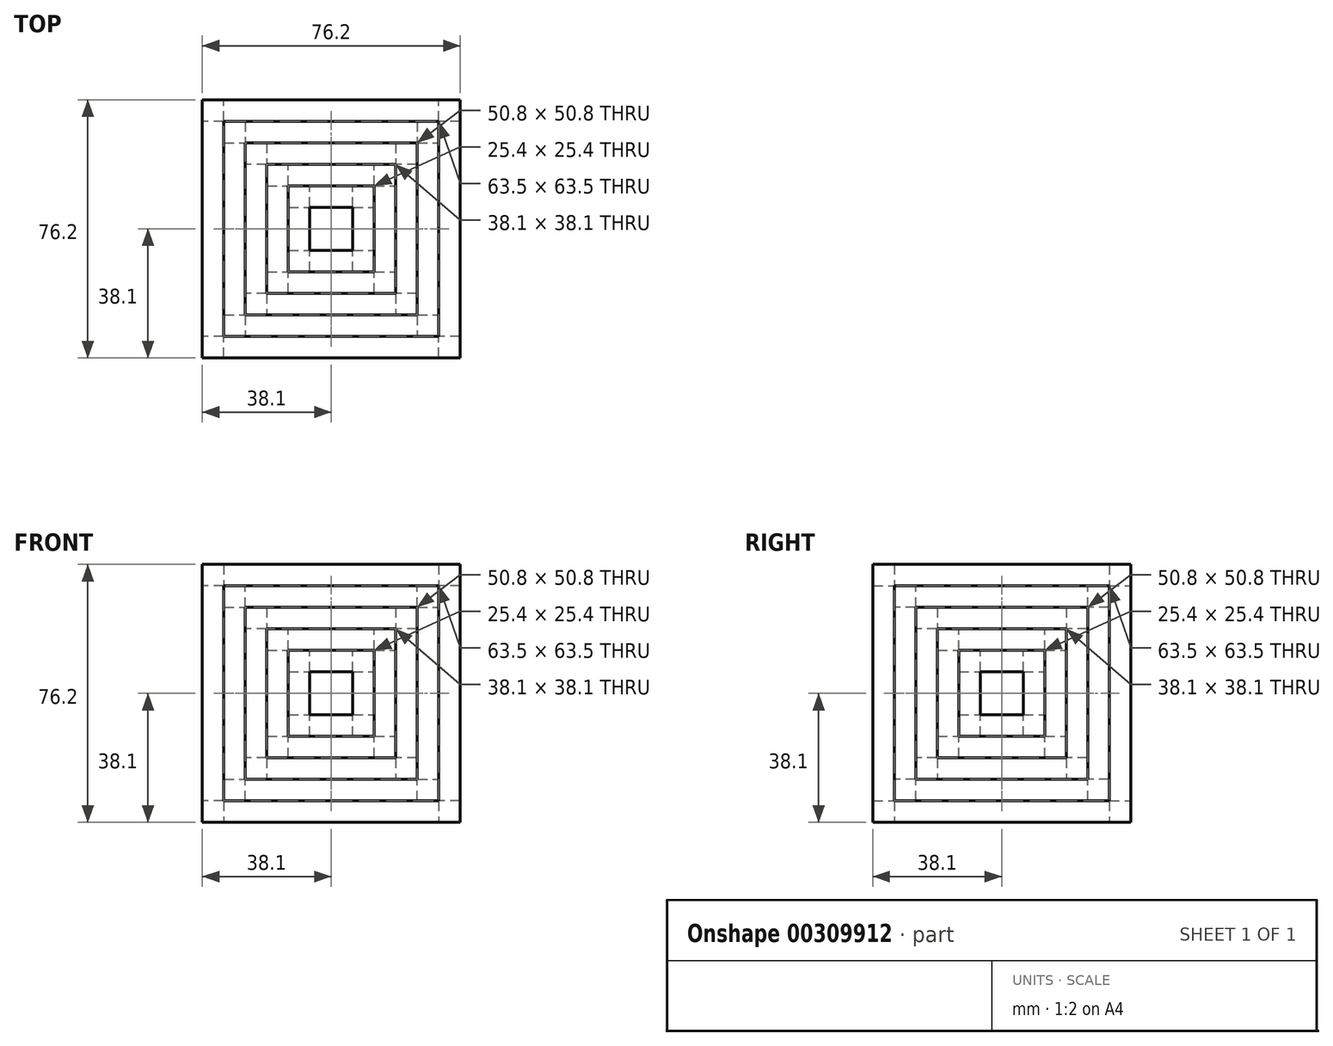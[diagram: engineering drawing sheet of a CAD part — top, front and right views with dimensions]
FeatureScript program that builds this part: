
annotation { "Feature Type Name" : "Feature", "Feature Type Description" : "" }
export const myFeature = defineFeature(function(context is Context, id is Id, definition is map)
    precondition{}
    {
        {
            var Q0;
            Q0=qCreatedBy(makeId("Top.planeOp"),FACE);
            var sketch = newSketch(context, id + "F0", { "sketchPlane" : qUnion([Q0])});
            skLineSegment(sketch, "E0.bottom", {"start": v(38.1, 38.1) * mm, "end": v(-38.1, 38.1) * mm});
            skLineSegment(sketch, "E0.top", {"start": v(38.1, -38.1) * mm, "end": v(-38.1, -38.1) * mm});
            skLineSegment(sketch, "E0.left", {"start": v(38.1, 38.1) * mm, "end": v(38.1, -38.1) * mm});
            skLineSegment(sketch, "E0.right", {"start": v(-38.1, 38.1) * mm, "end": v(-38.1, -38.1) * mm});
            skPoint(sketch, "E0.middle", {"position": v(0, 0) * mm});
            skSolve(sketch);
        }
        {
            var Q0;
            Q0=makeQuery(id+"F0.imprint","IMPRINT",FACE,{"disambiguationData":[TD([[makeQuery(id+"F0.imprint","IMPRINT",EDGE,{"derivedFrom":sQuery(id+"F0.wireOp",EDGE,"E0.bottom")}),1.0]])]});
            extrude(context, id + "F1", {"entities" : qUnion([Q0]), "endBound" : BoundingType.SYMMETRIC, "depth" : 76.2 * mm});
        }
        {
            var Q0;
            Q0=qCreatedBy(makeId("Right.planeOp"),FACE);
            var sketch = newSketch(context, id + "F2", { "sketchPlane" : qUnion([Q0])});
            skLineSegment(sketch, "E1.bottom", {"start": v(31.75, 31.75) * mm, "end": v(-31.75, 31.75) * mm});
            skLineSegment(sketch, "E1.top", {"start": v(31.75, -31.75) * mm, "end": v(-31.75, -31.75) * mm});
            skLineSegment(sketch, "E1.left", {"start": v(31.75, 31.75) * mm, "end": v(31.75, -31.75) * mm});
            skLineSegment(sketch, "E1.right", {"start": v(-31.75, 31.75) * mm, "end": v(-31.75, -31.75) * mm});
            skPoint(sketch, "E1.middle", {"position": v(0, 0) * mm});
            skSolve(sketch);
        }
        {
            var Q0;
            Q0=makeQuery(id+"F2.imprint","IMPRINT",FACE,{"disambiguationData":[TD([[makeQuery(id+"F2.imprint","IMPRINT",EDGE,{"derivedFrom":sQuery(id+"F2.wireOp",EDGE,"E1.bottom")}),1.0]])]});
            extrude(context, id + "F3", {"entities" : qUnion([Q0]), "operationType" : NewBodyOperationType.REMOVE, "endBound" : BoundingType.SYMMETRIC, "depth" : 76.2 * mm});
        }
        {
            var Q0;
            Q0=qCreatedBy(makeId("Front.planeOp"),FACE);
            var sketch = newSketch(context, id + "F4", { "sketchPlane" : qUnion([Q0])});
            skLineSegment(sketch, "E2.bottom", {"start": v(-31.75, 31.75) * mm, "end": v(31.75, 31.75) * mm});
            skLineSegment(sketch, "E2.top", {"start": v(-31.75, -31.75) * mm, "end": v(31.75, -31.75) * mm});
            skLineSegment(sketch, "E2.left", {"start": v(-31.75, 31.75) * mm, "end": v(-31.75, -31.75) * mm});
            skLineSegment(sketch, "E2.right", {"start": v(31.75, 31.75) * mm, "end": v(31.75, -31.75) * mm});
            skPoint(sketch, "E2.middle", {"position": v(0, 0) * mm});
            skSolve(sketch);
        }
        {
            var Q0;
            Q0=makeQuery(id+"F4.imprint","IMPRINT",FACE,{"disambiguationData":[TD([[makeQuery(id+"F4.imprint","IMPRINT",EDGE,{"derivedFrom":sQuery(id+"F4.wireOp",EDGE,"E2.bottom")}),-1.0]])]});
            extrude(context, id + "F5", {"entities" : qUnion([Q0]), "operationType" : NewBodyOperationType.REMOVE, "endBound" : BoundingType.SYMMETRIC, "depth" : 76.2 * mm});
        }
        {
            var Q0;
            Q0=qCreatedBy(makeId("Top.planeOp"),FACE);
            var sketch = newSketch(context, id + "F6", { "sketchPlane" : qUnion([Q0])});
            skLineSegment(sketch, "E3.bottom", {"start": v(31.75, 31.75) * mm, "end": v(-31.75, 31.75) * mm});
            skLineSegment(sketch, "E3.top", {"start": v(31.75, -31.75) * mm, "end": v(-31.75, -31.75) * mm});
            skLineSegment(sketch, "E3.left", {"start": v(31.75, 31.75) * mm, "end": v(31.75, -31.75) * mm});
            skLineSegment(sketch, "E3.right", {"start": v(-31.75, 31.75) * mm, "end": v(-31.75, -31.75) * mm});
            skPoint(sketch, "E3.middle", {"position": v(0, 0) * mm});
            skSolve(sketch);
        }
        {
            var Q0;
            Q0=makeQuery(id+"F6.imprint","IMPRINT",FACE,{"disambiguationData":[TD([[makeQuery(id+"F6.imprint","IMPRINT",EDGE,{"derivedFrom":sQuery(id+"F6.wireOp",EDGE,"E3.bottom")}),1.0]])]});
            extrude(context, id + "F7", {"entities" : qUnion([Q0]), "operationType" : NewBodyOperationType.REMOVE, "endBound" : BoundingType.SYMMETRIC, "depth" : 76.2 * mm});
        }
        {
            var Q0;
            Q0=makeQuery(id+"F6.imprint","IMPRINT",FACE,{"disambiguationData":[TD([[makeQuery(id+"F6.imprint","IMPRINT",EDGE,{"derivedFrom":sQuery(id+"F6.wireOp",EDGE,"E3.bottom")}),1.0]])]});
            extrude(context, id + "F8", {"entities" : qUnion([Q0]), "endBound" : BoundingType.SYMMETRIC, "depth" : 63.5 * mm});
        }
        {
            var Q0;
            Q0=qCreatedBy(makeId("Right.planeOp"),FACE);
            var sketch = newSketch(context, id + "F9", { "sketchPlane" : qUnion([Q0])});
            skLineSegment(sketch, "E4.bottom", {"start": v(-25.4, 25.4) * mm, "end": v(25.4, 25.4) * mm});
            skLineSegment(sketch, "E4.top", {"start": v(-25.4, -25.4) * mm, "end": v(25.4, -25.4) * mm});
            skLineSegment(sketch, "E4.left", {"start": v(-25.4, 25.4) * mm, "end": v(-25.4, -25.4) * mm});
            skLineSegment(sketch, "E4.right", {"start": v(25.4, 25.4) * mm, "end": v(25.4, -25.4) * mm});
            skPoint(sketch, "E4.middle", {"position": v(0, 0) * mm});
            skSolve(sketch);
        }
        {
            var Q0;
            Q0=makeQuery(id+"F9.imprint","IMPRINT",FACE,{"disambiguationData":[TD([[makeQuery(id+"F9.imprint","IMPRINT",EDGE,{"derivedFrom":sQuery(id+"F9.wireOp",EDGE,"E4.bottom")}),-1.0]])]});
            extrude(context, id + "F10", {"entities" : qUnion([Q0]), "operationType" : NewBodyOperationType.REMOVE, "endBound" : BoundingType.SYMMETRIC, "oppositeDirection" : true, "depth" : 63.5 * mm});
        }
        {
            var Q0;
            Q0=qCreatedBy(makeId("Front.planeOp"),FACE);
            var sketch = newSketch(context, id + "F11", { "sketchPlane" : qUnion([Q0])});
            skLineSegment(sketch, "E5.bottom", {"start": v(-25.4, 25.4) * mm, "end": v(25.4, 25.4) * mm});
            skLineSegment(sketch, "E5.top", {"start": v(-25.4, -25.4) * mm, "end": v(25.4, -25.4) * mm});
            skLineSegment(sketch, "E5.left", {"start": v(-25.4, 25.4) * mm, "end": v(-25.4, -25.4) * mm});
            skLineSegment(sketch, "E5.right", {"start": v(25.4, 25.4) * mm, "end": v(25.4, -25.4) * mm});
            skPoint(sketch, "E5.middle", {"position": v(0, 0) * mm});
            skSolve(sketch);
        }
        {
            var Q0;
            Q0 = qSketchRegion(id + "F11", true);
            extrude(context, id + "F12", {"entities" : qUnion([Q0]), "operationType" : NewBodyOperationType.REMOVE, "endBound" : BoundingType.SYMMETRIC, "oppositeDirection" : true, "depth" : 63.5 * mm});
        }
        {
            var Q0;
            Q0=qCreatedBy(makeId("Top.planeOp"),FACE);
            var sketch = newSketch(context, id + "F13", { "sketchPlane" : qUnion([Q0])});
            skLineSegment(sketch, "E6.bottom", {"start": v(25.4, -25.4) * mm, "end": v(-25.4, -25.4) * mm});
            skLineSegment(sketch, "E6.top", {"start": v(25.4, 25.4) * mm, "end": v(-25.4, 25.4) * mm});
            skLineSegment(sketch, "E6.left", {"start": v(25.4, -25.4) * mm, "end": v(25.4, 25.4) * mm});
            skLineSegment(sketch, "E6.right", {"start": v(-25.4, -25.4) * mm, "end": v(-25.4, 25.4) * mm});
            skPoint(sketch, "E6.middle", {"position": v(0, 0) * mm});
            skSolve(sketch);
        }
        {
            var Q0;
            Q0 = qSketchRegion(id + "F13", true);
            extrude(context, id + "F14", {"entities" : qUnion([Q0]), "operationType" : NewBodyOperationType.REMOVE, "endBound" : BoundingType.SYMMETRIC, "oppositeDirection" : true, "depth" : 63.5 * mm});
        }
        {
            var Q0;
            Q0 = qSketchRegion(id + "F13", true);
            extrude(context, id + "F15", {"entities" : qUnion([Q0]), "endBound" : BoundingType.SYMMETRIC, "depth" : 50.8 * mm});
        }
        {
            var Q0;
            Q0=qCreatedBy(makeId("Top.planeOp"),FACE);
            var sketch = newSketch(context, id + "F16", { "sketchPlane" : qUnion([Q0])});
            skLineSegment(sketch, "E7.bottom", {"start": v(19.05, -19.05) * mm, "end": v(-19.05, -19.05) * mm});
            skLineSegment(sketch, "E7.top", {"start": v(19.05, 19.05) * mm, "end": v(-19.05, 19.05) * mm});
            skLineSegment(sketch, "E7.left", {"start": v(19.05, -19.05) * mm, "end": v(19.05, 19.05) * mm});
            skLineSegment(sketch, "E7.right", {"start": v(-19.05, -19.05) * mm, "end": v(-19.05, 19.05) * mm});
            skPoint(sketch, "E7.middle", {"position": v(0, 0) * mm});
            skSolve(sketch);
        }
        {
            var Q0;
            Q0 = qSketchRegion(id + "F16", true);
            extrude(context, id + "F17", {"entities" : qUnion([Q0]), "operationType" : NewBodyOperationType.REMOVE, "endBound" : BoundingType.SYMMETRIC, "depth" : 50.8 * mm});
        }
        {
            var Q0;
            Q0=qCreatedBy(makeId("Right.planeOp"),FACE);
            var sketch = newSketch(context, id + "F18", { "sketchPlane" : qUnion([Q0])});
            skLineSegment(sketch, "E8.bottom", {"start": v(-19.05, 19.05) * mm, "end": v(19.05, 19.05) * mm});
            skLineSegment(sketch, "E8.top", {"start": v(-19.05, -19.05) * mm, "end": v(19.05, -19.05) * mm});
            skLineSegment(sketch, "E8.left", {"start": v(-19.05, 19.05) * mm, "end": v(-19.05, -19.05) * mm});
            skLineSegment(sketch, "E8.right", {"start": v(19.05, 19.05) * mm, "end": v(19.05, -19.05) * mm});
            skPoint(sketch, "E8.middle", {"position": v(0, 0) * mm});
            skSolve(sketch);
        }
        {
            var Q0;
            Q0 = qSketchRegion(id + "F18", true);
            extrude(context, id + "F19", {"entities" : qUnion([Q0]), "operationType" : NewBodyOperationType.REMOVE, "endBound" : BoundingType.SYMMETRIC, "depth" : 50.8 * mm});
        }
        {
            var Q0;
            Q0=qCreatedBy(makeId("Front.planeOp"),FACE);
            var sketch = newSketch(context, id + "F20", { "sketchPlane" : qUnion([Q0])});
            skLineSegment(sketch, "E9.bottom", {"start": v(19.05, 19.05) * mm, "end": v(-19.05, 19.05) * mm});
            skLineSegment(sketch, "E9.top", {"start": v(19.05, -19.05) * mm, "end": v(-19.05, -19.05) * mm});
            skLineSegment(sketch, "E9.left", {"start": v(19.05, 19.05) * mm, "end": v(19.05, -19.05) * mm});
            skLineSegment(sketch, "E9.right", {"start": v(-19.05, 19.05) * mm, "end": v(-19.05, -19.05) * mm});
            skPoint(sketch, "E9.middle", {"position": v(0, 0) * mm});
            skSolve(sketch);
        }
        {
            var Q0;
            Q0 = qSketchRegion(id + "F20", true);
            extrude(context, id + "F21", {"entities" : qUnion([Q0]), "operationType" : NewBodyOperationType.REMOVE, "endBound" : BoundingType.SYMMETRIC, "oppositeDirection" : true, "depth" : 50.8 * mm});
        }
        {
            var Q0;
            Q0 = qSketchRegion(id + "F20", true);
            extrude(context, id + "F22", {"entities" : qUnion([Q0]), "endBound" : BoundingType.SYMMETRIC, "depth" : 38.1 * mm});
        }
        {
            var Q0;
            Q0=qCreatedBy(makeId("Front.planeOp"),FACE);
            var sketch = newSketch(context, id + "F23", { "sketchPlane" : qUnion([Q0])});
            skLineSegment(sketch, "E10.bottom", {"start": v(-12.7, 12.7) * mm, "end": v(12.7, 12.7) * mm});
            skLineSegment(sketch, "E10.top", {"start": v(-12.7, -12.7) * mm, "end": v(12.7, -12.7) * mm});
            skLineSegment(sketch, "E10.left", {"start": v(-12.7, 12.7) * mm, "end": v(-12.7, -12.7) * mm});
            skLineSegment(sketch, "E10.right", {"start": v(12.7, 12.7) * mm, "end": v(12.7, -12.7) * mm});
            skPoint(sketch, "E10.middle", {"position": v(0, 0) * mm});
            skSolve(sketch);
        }
        {
            var Q0;
            Q0 = qSketchRegion(id + "F23", true);
            extrude(context, id + "F24", {"entities" : qUnion([Q0]), "operationType" : NewBodyOperationType.REMOVE, "endBound" : BoundingType.SYMMETRIC, "depth" : 38.1 * mm});
        }
        {
            var Q0;
            Q0=qCreatedBy(makeId("Right.planeOp"),FACE);
            var sketch = newSketch(context, id + "F25", { "sketchPlane" : qUnion([Q0])});
            skLineSegment(sketch, "E11.bottom", {"start": v(-12.7, 12.7) * mm, "end": v(12.7, 12.7) * mm});
            skLineSegment(sketch, "E11.top", {"start": v(-12.7, -12.7) * mm, "end": v(12.7, -12.7) * mm});
            skLineSegment(sketch, "E11.left", {"start": v(-12.7, 12.7) * mm, "end": v(-12.7, -12.7) * mm});
            skLineSegment(sketch, "E11.right", {"start": v(12.7, 12.7) * mm, "end": v(12.7, -12.7) * mm});
            skPoint(sketch, "E11.middle", {"position": v(0, 0) * mm});
            skSolve(sketch);
        }
        {
            var Q0;
            Q0 = qSketchRegion(id + "F25", true);
            extrude(context, id + "F26", {"entities" : qUnion([Q0]), "operationType" : NewBodyOperationType.REMOVE, "endBound" : BoundingType.SYMMETRIC, "oppositeDirection" : true, "depth" : 38.1 * mm});
        }
        {
            var Q0;
            Q0=makeQuery(id+"F22.opExtrude","SWEPT_FACE",FACE,{"disambiguationData":[OSD([sQuery(id+"F20.wireOp",EDGE,"E9.top")])]});
            var sketch = newSketch(context, id + "F27", { "sketchPlane" : qUnion([Q0])});
            skLineSegment(sketch, "E12.bottom", {"start": v(-12.7, 12.7) * mm, "end": v(12.7, 12.7) * mm});
            skLineSegment(sketch, "E12.top", {"start": v(-12.7, -12.7) * mm, "end": v(12.7, -12.7) * mm});
            skLineSegment(sketch, "E12.left", {"start": v(-12.7, 12.7) * mm, "end": v(-12.7, -12.7) * mm});
            skLineSegment(sketch, "E12.right", {"start": v(12.7, 12.7) * mm, "end": v(12.7, -12.7) * mm});
            skPoint(sketch, "E12.middle", {"position": v(0, 0) * mm});
            skSolve(sketch);
        }
        {
            var Q0;
            Q0 = qSketchRegion(id + "F27", true);
            extrude(context, id + "F28", {"entities" : qUnion([Q0]), "operationType" : NewBodyOperationType.REMOVE, "endBound" : BoundingType.SYMMETRIC, "depth" : 127 * mm});
        }
        {
            var Q0;
            Q0 = qSketchRegion(id + "F25", true);
            extrude(context, id + "F29", {"entities" : qUnion([Q0]), "endBound" : BoundingType.SYMMETRIC, "depth" : 25.4 * mm});
        }
        {
            var Q0;
            Q0=qCreatedBy(makeId("Front.planeOp"),FACE);
            var sketch = newSketch(context, id + "F30", { "sketchPlane" : qUnion([Q0])});
            skLineSegment(sketch, "E13.bottom", {"start": v(6.35, 6.35) * mm, "end": v(-6.35, 6.35) * mm});
            skLineSegment(sketch, "E13.top", {"start": v(6.35, -6.35) * mm, "end": v(-6.35, -6.35) * mm});
            skLineSegment(sketch, "E13.left", {"start": v(6.35, 6.35) * mm, "end": v(6.35, -6.35) * mm});
            skLineSegment(sketch, "E13.right", {"start": v(-6.35, 6.35) * mm, "end": v(-6.35, -6.35) * mm});
            skPoint(sketch, "E13.middle", {"position": v(0, 0) * mm});
            skSolve(sketch);
        }
        {
            var Q0;
            Q0 = qSketchRegion(id + "F30", true);
            extrude(context, id + "F31", {"entities" : qUnion([Q0]), "operationType" : NewBodyOperationType.REMOVE, "endBound" : BoundingType.SYMMETRIC, "depth" : 25.4 * mm});
        }
        {
            var Q0;
            Q0=qCreatedBy(makeId("Right.planeOp"),FACE);
            var sketch = newSketch(context, id + "F32", { "sketchPlane" : qUnion([Q0])});
            skLineSegment(sketch, "E14.bottom", {"start": v(-6.35, 6.35) * mm, "end": v(6.35, 6.35) * mm});
            skLineSegment(sketch, "E14.top", {"start": v(-6.35, -6.35) * mm, "end": v(6.35, -6.35) * mm});
            skLineSegment(sketch, "E14.left", {"start": v(-6.35, 6.35) * mm, "end": v(-6.35, -6.35) * mm});
            skLineSegment(sketch, "E14.right", {"start": v(6.35, 6.35) * mm, "end": v(6.35, -6.35) * mm});
            skPoint(sketch, "E14.middle", {"position": v(0, 0) * mm});
            skSolve(sketch);
        }
        {
            var Q0;
            Q0 = qSketchRegion(id + "F32", true);
            extrude(context, id + "F33", {"entities" : qUnion([Q0]), "operationType" : NewBodyOperationType.REMOVE, "endBound" : BoundingType.SYMMETRIC, "oppositeDirection" : true, "depth" : 25.4 * mm});
        }
        {
            var Q0;
            Q0=qCreatedBy(makeId("Top.planeOp"),FACE);
            var sketch = newSketch(context, id + "F34", { "sketchPlane" : qUnion([Q0])});
            skLineSegment(sketch, "E15.bottom", {"start": v(6.35, 6.35) * mm, "end": v(-6.35, 6.35) * mm});
            skLineSegment(sketch, "E15.top", {"start": v(6.35, -6.35) * mm, "end": v(-6.35, -6.35) * mm});
            skLineSegment(sketch, "E15.left", {"start": v(6.35, 6.35) * mm, "end": v(6.35, -6.35) * mm});
            skLineSegment(sketch, "E15.right", {"start": v(-6.35, 6.35) * mm, "end": v(-6.35, -6.35) * mm});
            skPoint(sketch, "E15.middle", {"position": v(0, 0) * mm});
            skSolve(sketch);
        }
        {
            var Q0;
            Q0 = qSketchRegion(id + "F34", true);
            extrude(context, id + "F35", {"entities" : qUnion([Q0]), "operationType" : NewBodyOperationType.REMOVE, "endBound" : BoundingType.SYMMETRIC, "oppositeDirection" : true, "depth" : 25.4 * mm});
        }
        {
            var Q0;
            Q0 = qSketchRegion(id + "F34", true);
            extrude(context, id + "F36", {"entities" : qUnion([Q0]), "endBound" : BoundingType.SYMMETRIC, "depth" : 12.7 * mm});
        }
    });
